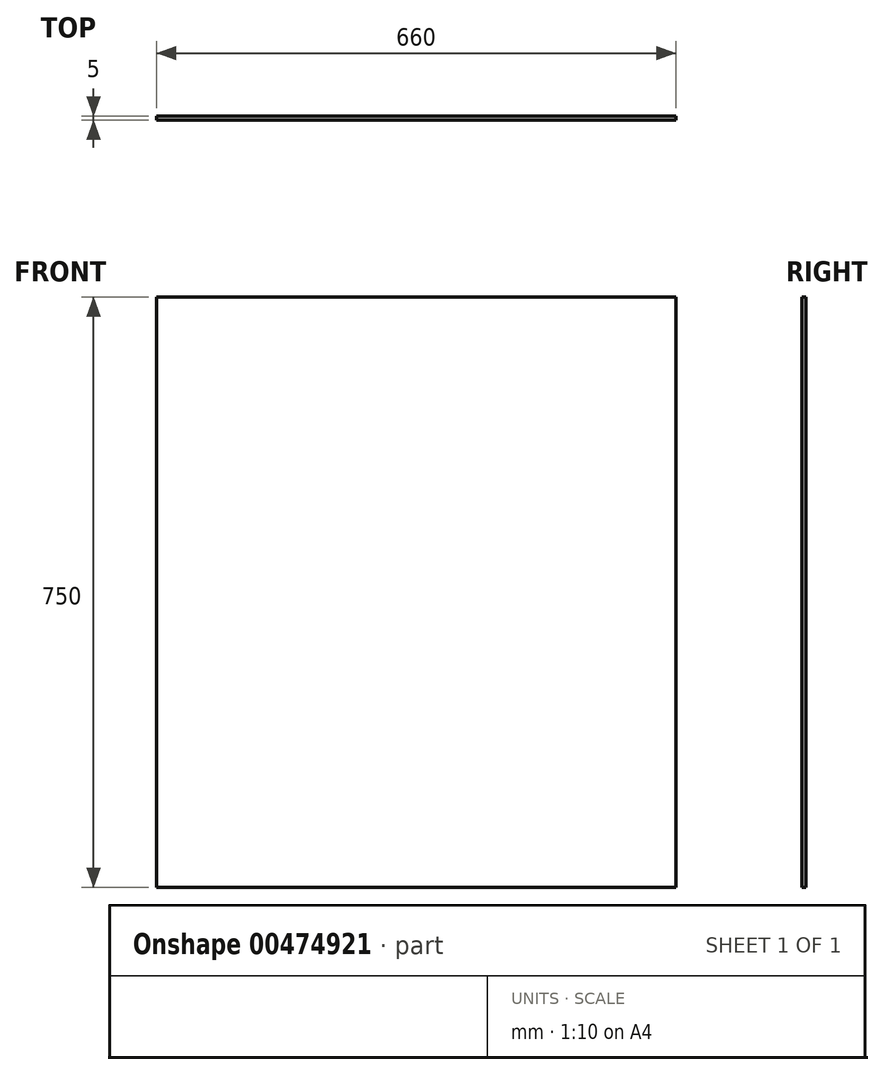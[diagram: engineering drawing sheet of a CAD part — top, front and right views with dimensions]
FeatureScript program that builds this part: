
annotation { "Feature Type Name" : "Feature", "Feature Type Description" : "" }
export const myFeature = defineFeature(function(context is Context, id is Id, definition is map)
    precondition{}
    {
        {
            var Q0;
            Q0=qCreatedBy(makeId("Front.planeOp"),FACE);
            var sketch = newSketch(context, id + "F0", { "sketchPlane" : qUnion([Q0])});
            skLineSegment(sketch, "E0.bottom", {"start": v(-279.26, 520.08) * mm, "end": v(380.74, 520.08) * mm});
            skLineSegment(sketch, "E0.top", {"start": v(-279.26, -229.92) * mm, "end": v(380.74, -229.92) * mm});
            skLineSegment(sketch, "E0.left", {"start": v(-279.26, 520.08) * mm, "end": v(-279.26, -229.92) * mm});
            skLineSegment(sketch, "E0.right", {"start": v(380.74, 520.08) * mm, "end": v(380.74, -229.92) * mm});
            skPoint(sketch, "E1.endSnap0", {"position": v(50.74, 520.08) * mm});
            skSolve(sketch);
        }
        {
            var Q0;
            Q0=makeQuery(id+"F0.imprint","IMPRINT",FACE,{"disambiguationData":[TD([[makeQuery(id+"F0.imprint","IMPRINT",EDGE,{"derivedFrom":sQuery(id+"F0.wireOp",EDGE,"E0.bottom")}),-1.0]])]});
            extrude(context, id + "F1", {"entities" : qUnion([Q0]), "depth" : 5 * mm});
        }
    });
